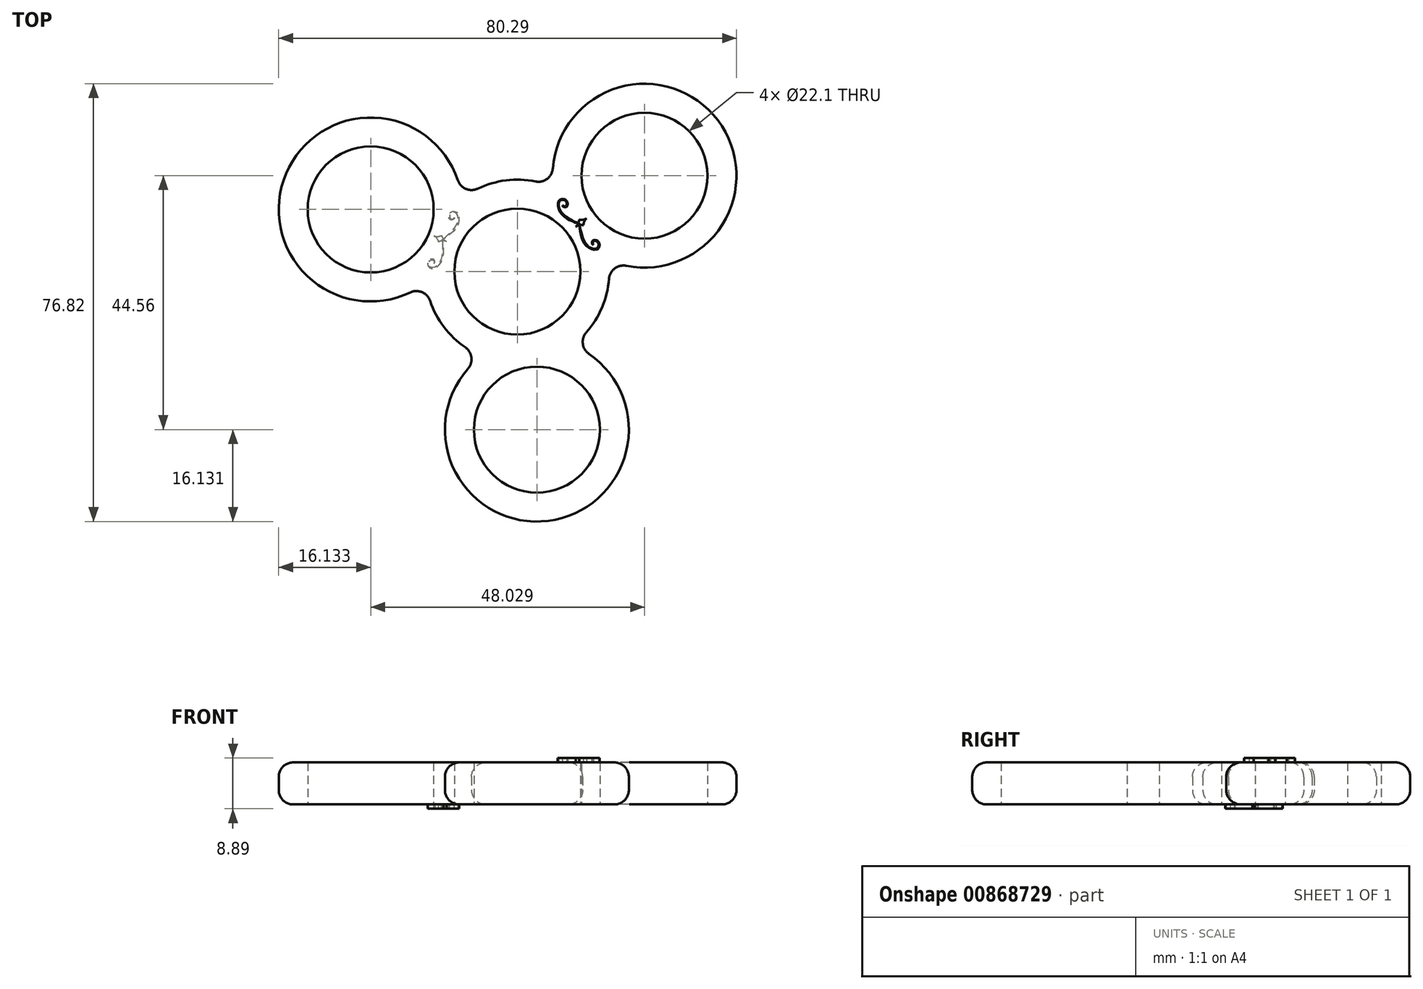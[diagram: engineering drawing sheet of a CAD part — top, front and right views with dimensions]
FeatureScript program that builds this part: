
annotation { "Feature Type Name" : "Feature", "Feature Type Description" : "" }
export const myFeature = defineFeature(function(context is Context, id is Id, definition is map)
    precondition{}
    {
        {
            var Q0;
            Q0=qCreatedBy(makeId("Top.planeOp"),FACE);
            var sketch = newSketch(context, id + "F0", { "sketchPlane" : qUnion([Q0])});
            skCircle(sketch, "E0", {"center": v(0, 0) * mm, "radius": 11.05 * mm});
            skCircle(sketch, "E1", {"center": v(22.3, 16.83) * mm, "radius": 11.05 * mm});
            skCircle(sketch, "E2.1.1", {"center": v(-25.73, 10.9) * mm, "radius": 11.05 * mm});
            skCircle(sketch, "E2.2.1", {"center": v(3.42, -27.73) * mm, "radius": 11.05 * mm});
            skArc(sketch, "E3.0", {"start": v(-10.44, 16.04) * mm, "mid": v(-40.58, 17.2) * mm, "end": v(-18.79, -3.66) * mm});
            skArc(sketch, "E4.0", {"start": v(-8.67, -17.06) * mm, "mid": v(5.4, -43.74) * mm, "end": v(12.56, -14.44) * mm});
            skArc(sketch, "E5.0", {"start": v(19.11, 1.02) * mm, "mid": v(35.18, 26.55) * mm, "end": v(6.22, 18.1) * mm});
            skArc(sketch, "E6.0", {"start": v(-15.29, -5.14) * mm, "mid": v(-12.87, -9.72) * mm, "end": v(-9.14, -13.29) * mm});
            skArc(sketch, "E7.trimOffspring", {"start": v(3.19, 15.81) * mm, "mid": v(-1.98, 16) * mm, "end": v(-6.94, 14.56) * mm});
            skArc(sketch, "E8.trimOffspring", {"start": v(12.1, -10.67) * mm, "mid": v(14.85, -6.3) * mm, "end": v(16.08, -1.27) * mm});
            skPoint(sketch, "E9.visualSharp", {"position": v(-9.72, 12.87) * mm});
            skArc(sketch, "E9.filletArc", {"start": v(-10.44, 16.04) * mm, "mid": v(-9.02, 14.51) * mm, "end": v(-6.94, 14.56) * mm});
            skPoint(sketch, "E10.visualSharp", {"position": v(6.3, 14.85) * mm});
            skArc(sketch, "E10.filletArc", {"start": v(3.19, 15.81) * mm, "mid": v(5.22, 16.27) * mm, "end": v(6.22, 18.1) * mm});
            skPoint(sketch, "E11.visualSharp", {"position": v(16, 1.98) * mm});
            skArc(sketch, "E11.filletArc", {"start": v(19.11, 1.02) * mm, "mid": v(17.08, 0.56) * mm, "end": v(16.08, -1.27) * mm});
            skPoint(sketch, "E12.visualSharp", {"position": v(-16, -1.97) * mm});
            skArc(sketch, "E12.filletArc", {"start": v(-15.29, -5.14) * mm, "mid": v(-16.7, -3.61) * mm, "end": v(-18.79, -3.66) * mm});
            skPoint(sketch, "E13.visualSharp", {"position": v(-6.29, -14.85) * mm});
            skArc(sketch, "E13.filletArc", {"start": v(-8.67, -17.06) * mm, "mid": v(-8.06, -15.07) * mm, "end": v(-9.14, -13.29) * mm});
            skPoint(sketch, "E14.visualSharp", {"position": v(9.71, -12.88) * mm});
            skArc(sketch, "E14.filletArc", {"start": v(12.1, -10.67) * mm, "mid": v(11.48, -12.66) * mm, "end": v(12.56, -14.44) * mm});
            skSolve(sketch);
        }
        {
            var Q0;
            Q0=makeQuery(id+"F0.imprint","IMPRINT",FACE,{"disambiguationData":[TD([[makeQuery(id+"F0.imprint","IMPRINT",EDGE,{"derivedFrom":sQuery(id+"F0.wireOp",EDGE,"E1")}),-1.0]])]});
            extrude(context, id + "F1", {"entities" : qUnion([Q0]), "depth" : 7.37 * mm, "offsetDistance" : 25.4 * mm});
        }
        {
            var Q0;
            Q0=makeQuery(id+"F1.opExtrude","CAP_EDGE",EDGE,{"disambiguationData":[OSD([sQuery(id+"F0.wireOp",EDGE,"E3.0")])],"isStart":false});
            var Q1;
            Q1=makeQuery(id+"F1.opExtrude","CAP_EDGE",EDGE,{"disambiguationData":[OSD([sQuery(id+"F0.wireOp",EDGE,"E3.0")])],"isStart":true});
            fillet(context, id + "F2", {"entities" : qUnion([Q0, Q1]), "radius" : 2.54 * mm, "tangentPropagation" : true, "allowEdgeOverflow" : false});
        }
        {
            var Q0;
            Q0=makeQuery(id+"F1.opExtrude","CAP_FACE",FACE,{"disambiguationData":[OSD([sQuery(id+"F0.wireOp",EDGE,"E1"),sQuery(id+"F0.wireOp",EDGE,"E2.1.1"),sQuery(id+"F0.wireOp",EDGE,"E0"),sQuery(id+"F0.wireOp",EDGE,"E2.2.1"),sQuery(id+"F0.wireOp",EDGE,"E3.0"),sQuery(id+"F0.wireOp",EDGE,"E4.0"),sQuery(id+"F0.wireOp",EDGE,"E5.0"),sQuery(id+"F0.wireOp",EDGE,"E6.0"),sQuery(id+"F0.wireOp",EDGE,"E7.trimOffspring"),sQuery(id+"F0.wireOp",EDGE,"E8.trimOffspring"),sQuery(id+"F0.wireOp",EDGE,"E9.filletArc"),sQuery(id+"F0.wireOp",EDGE,"E10.filletArc"),sQuery(id+"F0.wireOp",EDGE,"E11.filletArc"),sQuery(id+"F0.wireOp",EDGE,"E12.filletArc"),sQuery(id+"F0.wireOp",EDGE,"E13.filletArc"),sQuery(id+"F0.wireOp",EDGE,"E14.filletArc")])],"isStart":false});
            var sketch = newSketch(context, id + "F3", { "sketchPlane" : qUnion([Q0])});
            skFitSpline(sketch, "E15.MirrorCS", {"points": [v(10.96, 8.33) * mm, v(9.5, 9.05) * mm, v(7.51, 10.76) * mm, v(7.43, 12.32) * mm, v(8.25, 12.53) * mm, v(8.68, 11.94) * mm, v(8.48, 11.48) * mm, v(7.92, 11.65) * mm], "startDerivative": vector(-7.93, 3.64) * mm, "endDerivative": vector(-5.3, 5.44) * mm});
            skArc(sketch, "E16", {"start": v(10.84, 9.12) * mm, "mid": v(11.52, 9.1) * mm, "end": v(12.15, 9.35) * mm});
            skArc(sketch, "E17", {"start": v(10.23, 7.86) * mm, "mid": v(10.67, 8.43) * mm, "end": v(10.84, 9.12) * mm});
            skFitSpline(sketch, "E18", {"points": [v(7.92, 11.65) * mm, v(7.95, 11.46) * mm, v(8.19, 11.31) * mm, v(8.7, 11.42) * mm, v(8.76, 12.25) * mm, v(8.06, 12.74) * mm, v(7.25, 12.4) * mm, v(7.35, 10.68) * mm, v(8.95, 9.16) * mm, v(10.96, 8.33) * mm], "startDerivative": vector(0.04, -4.02) * mm, "endDerivative": vector(12.52, -4.03) * mm});
            skArc(sketch, "E19.MirrorCS", {"start": v(11.6, 8.14) * mm, "mid": v(11.75, 8.8) * mm, "end": v(12.15, 9.35) * mm});
            skArc(sketch, "E20.MirrorCS", {"start": v(10.23, 7.86) * mm, "mid": v(10.89, 8.14) * mm, "end": v(11.6, 8.14) * mm});
            skFitSpline(sketch, "E21.MirrorCS", {"points": [v(10.87, 8.45) * mm, v(11.21, 6.86) * mm, v(12.37, 4.51) * mm, v(13.86, 4.04) * mm, v(14.27, 4.8) * mm, v(13.8, 5.35) * mm, v(13.3, 5.27) * mm, v(13.33, 4.68) * mm], "startDerivative": vector(1.57, -8.58) * mm, "endDerivative": vector(3.97, -6.47) * mm});
            skFitSpline(sketch, "E22.MirrorCS", {"points": [v(13.33, 4.68) * mm, v(13.16, 4.76) * mm, v(13.07, 5.03) * mm, v(13.3, 5.5) * mm, v(14.13, 5.35) * mm, v(14.43, 4.55) * mm, v(13.9, 3.85) * mm, v(12.26, 4.37) * mm, v(11.17, 6.3) * mm, v(10.87, 8.45) * mm], "startDerivative": vector(-3.88, 1.03) * mm, "endDerivative": vector(-0.82, 13.13) * mm});
            skSolve(sketch);
        }
        {
            var Q0;
            Q0 = qSketchRegion(id + "F3", true);
            extrude(context, id + "F4", {"entities" : qUnion([Q0]), "operationType" : NewBodyOperationType.ADD, "depth" : 0.76 * mm, "offsetDistance" : 25.4 * mm});
        }
        {
            var Q0;
            Q0=makeQuery(id+"F1.opExtrude","CAP_FACE",FACE,{"disambiguationData":[OSD([sQuery(id+"F0.wireOp",EDGE,"E1"),sQuery(id+"F0.wireOp",EDGE,"E2.1.1"),sQuery(id+"F0.wireOp",EDGE,"E0"),sQuery(id+"F0.wireOp",EDGE,"E2.2.1"),sQuery(id+"F0.wireOp",EDGE,"E3.0"),sQuery(id+"F0.wireOp",EDGE,"E4.0"),sQuery(id+"F0.wireOp",EDGE,"E5.0"),sQuery(id+"F0.wireOp",EDGE,"E6.0"),sQuery(id+"F0.wireOp",EDGE,"E7.trimOffspring"),sQuery(id+"F0.wireOp",EDGE,"E8.trimOffspring"),sQuery(id+"F0.wireOp",EDGE,"E9.filletArc"),sQuery(id+"F0.wireOp",EDGE,"E10.filletArc"),sQuery(id+"F0.wireOp",EDGE,"E11.filletArc"),sQuery(id+"F0.wireOp",EDGE,"E12.filletArc"),sQuery(id+"F0.wireOp",EDGE,"E13.filletArc"),sQuery(id+"F0.wireOp",EDGE,"E14.filletArc")])],"isStart":true});
            var sketch = newSketch(context, id + "F5", { "sketchPlane" : qUnion([Q0])});
            skFitSpline(sketch, "E23.MirrorCS", {"points": [v(-13.22, -5.55) * mm, v(-11.99, -6.6) * mm, v(-10.46, -8.74) * mm, v(-10.75, -10.28) * mm, v(-11.6, -10.28) * mm, v(-11.87, -9.6) * mm, v(-11.57, -9.2) * mm, v(-11.07, -9.5) * mm], "startDerivative": vector(6.82, -5.44) * mm, "endDerivative": vector(3.83, -6.56) * mm});
            skArc(sketch, "E24", {"start": v(-13.3, -6.35) * mm, "mid": v(-13.95, -6.16) * mm, "end": v(-14.62, -6.25) * mm});
            skArc(sketch, "E25", {"start": v(-12.4, -5.27) * mm, "mid": v(-12.96, -5.72) * mm, "end": v(-13.3, -6.35) * mm});
            skFitSpline(sketch, "E26", {"points": [v(-11.07, -9.5) * mm, v(-11.05, -9.31) * mm, v(-11.25, -9.11) * mm, v(-11.77, -9.1) * mm, v(-12.03, -9.89) * mm, v(-11.47, -10.53) * mm, v(-10.6, -10.4) * mm, v(-10.28, -8.7) * mm, v(-11.47, -6.84) * mm, v(-13.22, -5.55) * mm], "startDerivative": vector(0.92, 3.9) * mm, "endDerivative": vector(-11.18, 6.93) * mm});
            skArc(sketch, "E27.MirrorCS", {"start": v(-13.8, -5.22) * mm, "mid": v(-14.1, -5.82) * mm, "end": v(-14.62, -6.25) * mm});
            skArc(sketch, "E28.MirrorCS", {"start": v(-12.4, -5.27) * mm, "mid": v(-13.1, -5.39) * mm, "end": v(-13.8, -5.22) * mm});
            skFitSpline(sketch, "E29.MirrorCS", {"points": [v(-13.16, -5.69) * mm, v(-13.11, -4.07) * mm, v(-13.67, -1.5) * mm, v(-15, -0.7) * mm, v(-15.58, -1.32) * mm, v(-15.26, -1.97) * mm, v(-14.76, -2.02) * mm, v(-14.64, -1.44) * mm], "startDerivative": vector(0.54, 8.7) * mm, "endDerivative": vector(-2.3, 7.24) * mm});
            skFitSpline(sketch, "E30.MirrorCS", {"points": [v(-14.64, -1.44) * mm, v(-14.5, -1.56) * mm, v(-14.48, -1.84) * mm, v(-14.81, -2.24) * mm, v(-15.58, -1.9) * mm, v(-15.68, -1.05) * mm, v(-15, -0.5) * mm, v(-13.52, -1.4) * mm, v(-12.94, -3.53) * mm, v(-13.16, -5.69) * mm], "startDerivative": vector(3.52, -1.94) * mm, "endDerivative": vector(-2.37, -12.94) * mm});
            skSolve(sketch);
        }
        {
            var Q0;
            Q0 = qSketchRegion(id + "F5", true);
            extrude(context, id + "F6", {"entities" : qUnion([Q0]), "operationType" : NewBodyOperationType.ADD, "depth" : 0.76 * mm, "offsetDistance" : 25.4 * mm});
        }
    });
